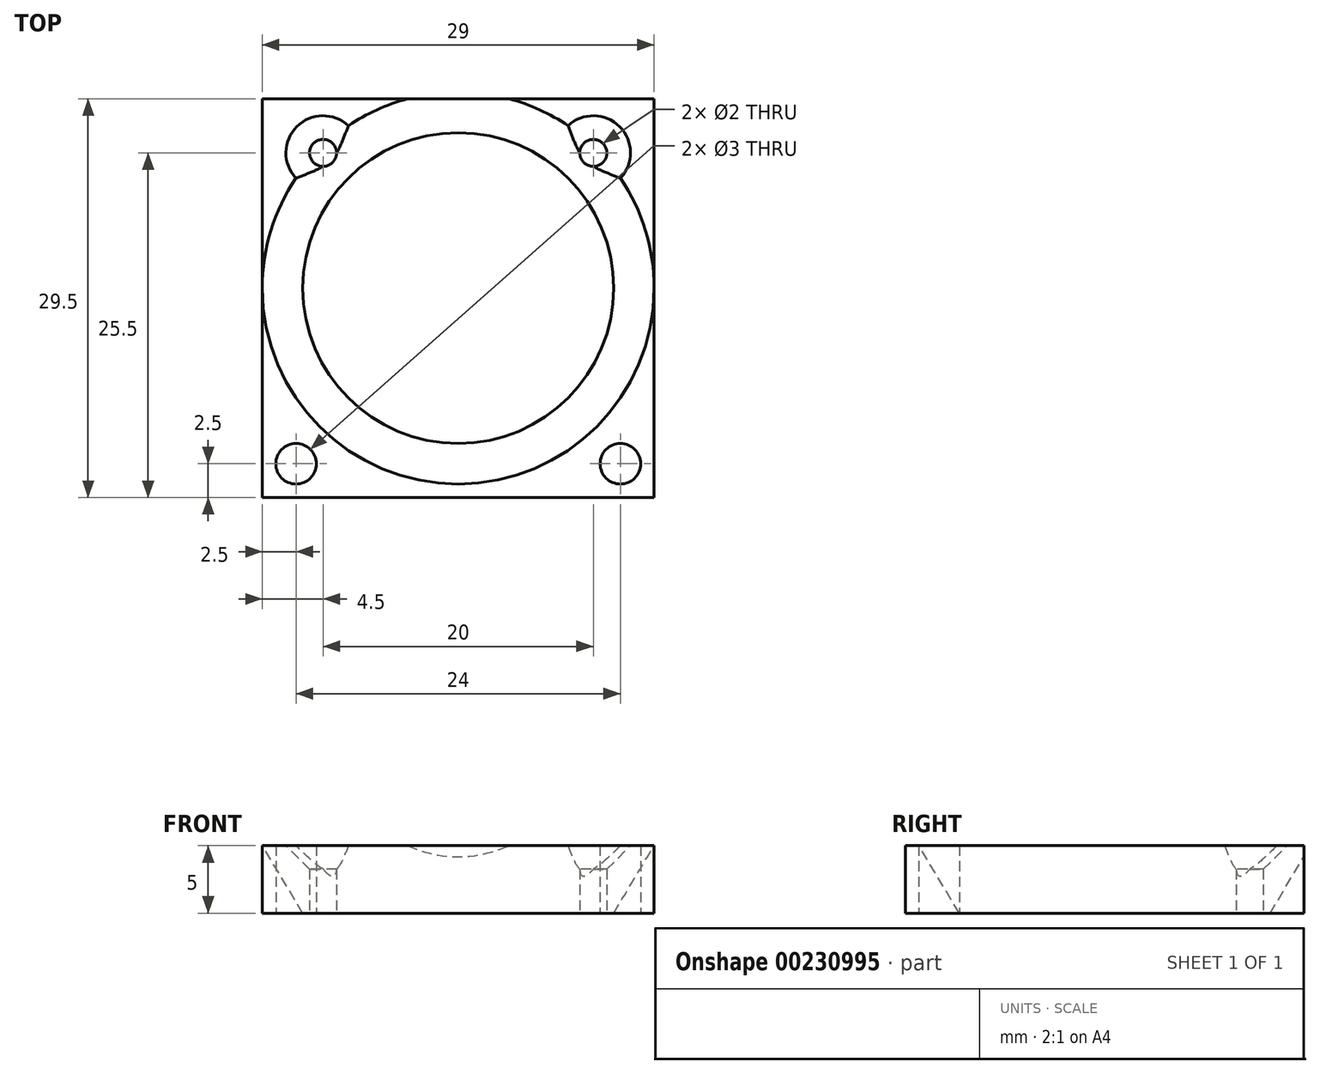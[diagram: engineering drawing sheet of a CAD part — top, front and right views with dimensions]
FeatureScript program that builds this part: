
annotation { "Feature Type Name" : "Feature", "Feature Type Description" : "" }
export const myFeature = defineFeature(function(context is Context, id is Id, definition is map)
    precondition{}
    {
        {
            var Q0;
            Q0=qCreatedBy(makeId("Top.planeOp"),FACE);
            var sketch = newSketch(context, id + "F0", { "sketchPlane" : qUnion([Q0])});
            skCircle(sketch, "E0", {"center": v(0, 0) * mm, "radius": 11.5 * mm});
            skCircle(sketch, "E1", {"center": v(10, 10) * mm, "radius": 1 * mm});
            skCircle(sketch, "E2", {"center": v(-10, 10) * mm, "radius": 1 * mm});
            skLineSegment(sketch, "E3", {"start": v(-14.5, 14) * mm, "end": v(14.5, 14) * mm});
            skCircle(sketch, "E4", {"center": v(-12, -13) * mm, "radius": 1.5 * mm});
            skCircle(sketch, "E5", {"center": v(12, -13) * mm, "radius": 1.5 * mm});
            skLineSegment(sketch, "E6", {"start": v(-14.5, 14) * mm, "end": v(-14.5, -15.5) * mm});
            skLineSegment(sketch, "E7", {"start": v(14.5, 14) * mm, "end": v(14.5, -15.5) * mm});
            skLineSegment(sketch, "E8", {"start": v(-14.5, -15.5) * mm, "end": v(14.5, -15.5) * mm});
            skSolve(sketch);
        }
        {
            var Q0;
            Q0=makeQuery(id+"F0.imprint","IMPRINT",FACE,{"disambiguationData":[TD([[makeQuery(id+"F0.imprint","IMPRINT",EDGE,{"derivedFrom":sQuery(id+"F0.wireOp",EDGE,"E0")}),-1.0]])]});
            extrude(context, id + "F1", {"entities" : qUnion([Q0]), "depth" : 5 * mm});
        }
        {
            var Q0;
            Q0=qCreatedBy(makeId("Right.planeOp"),FACE);
            var sketch = newSketch(context, id + "F2", { "sketchPlane" : qUnion([Q0])});
            skLineSegment(sketch, "E9.0", {"start": v(-15.5, 5) * mm, "end": v(-15.5, 0) * mm});
            skLineSegment(sketch, "E10.0", {"start": v(14, 5) * mm, "end": v(14, 0) * mm});
            skLineSegment(sketch, "E11", {"start": v(-11.5, 0) * mm, "end": v(-11.5, 5) * mm});
            skLineSegment(sketch, "E12", {"start": v(11.5, 5) * mm, "end": v(11.5, 0) * mm});
            skLineSegment(sketch, "E13", {"start": v(0, 0) * mm, "end": v(0, 12.72) * mm});
            skLineSegment(sketch, "E14", {"start": v(-11.5, 0) * mm, "end": v(-14.5, 5) * mm});
            skLineSegment(sketch, "E15", {"start": v(-14.5, 5) * mm, "end": v(-11.5, 5) * mm});
            skSolve(sketch);
        }
        {
            var Q0;
            Q0=makeQuery(id+"F2.imprint","IMPRINT",FACE,{"disambiguationData":[TD([[makeQuery(id+"F2.imprint","IMPRINT",EDGE,{"derivedFrom":sQuery(id+"F2.wireOp",EDGE,"E11")}),1.0]])]});
            var Q1;
            Q1=sQuery(id+"F2.wireOp",EDGE,"E13");
            revolve(context, id + "F3", {"operationType" : NewBodyOperationType.REMOVE, "entities" : qUnion([Q0]), "axis" : qUnion([Q1]), "revolveType" : RevolveType.FULL, "oppositeDirection" : true});
        }
        {
            var Q0;
            Q0=makeQuery(id+"F1.opExtrude","CAP_EDGE",EDGE,{"disambiguationData":[OSD([sQuery(id+"F0.wireOp",EDGE,"E2")])],"isStart":false});
            var Q1;
            Q1=makeQuery(id+"F1.opExtrude","CAP_EDGE",EDGE,{"disambiguationData":[OSD([sQuery(id+"F0.wireOp",EDGE,"E1")])],"isStart":false});
            chamfer(context, id + "F4", {"entities" : qUnion([Q0, Q1]), "width" : 1.75 * mm, "tangentPropagation" : true});
        }
    });
